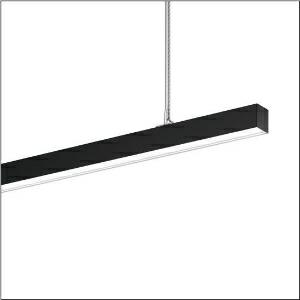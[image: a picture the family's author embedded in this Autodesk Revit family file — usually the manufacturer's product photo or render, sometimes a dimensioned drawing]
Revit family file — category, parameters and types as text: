
# Revit family: silica_21_51mx33da47bb
name_source: partatom
category: Lighting Fixtures
units: mm (PartAtom-declared; Revit-internal decimal feet)

## family parameters
Cut with Voids When Loaded = No
Host = Face
Light Source = No
Part Type = Normal
Room Calculation Point = No
Round Connector Dimension = Use Diameter
Shared = No

## types (1)
- --- (1 x LED, 5910 lm, 38.4 W, 4000K)
    Apparent Load = 38 VA
    CIE Flux Codes = 78 96 99 55 100
    Color Rendering = 80
    Color Temperature = 4000K
    Default Elevation = 1800 mm
    Description = Silica 21, office luminaire, primary optical cover: prismatic diffuser, of PMMA, CAT 2 (L<= 3000cd/m²), light emission: direct/indirect distribution, primary light characteristic: symmetric, installation type: suspended mounting, LED, rated luminous flux: 5.910lm, luminous efficacy: 154lm/W, light colour: 840, colour temperature: 4000K, control gear: DALI 2, with terminal, 3+2-pole, max. 2.5mm², mains connection: 220..240V, AC, 50/60Hz, rated input power: 38.4W, luminaire housing, of aluminium, matt jet black (RAL 9005), length: 1.204mm, width: 53mm, height: 53mm, protection rating (complete): IP20, insulation class (complete): insulation class I (protective earthing), certification: CE, permissible operating ambient temperature: 0..+35°C, standard: EN 50419, packaging unit: 1 piece
    Height = 53 mm
    Lamp = 1 x LED
    Lamp Light Flux = 5910 lm
    Lamp Power = 38.4 W
    Lamp count = 1
    Length = 1204 mm
    Luminous efficacy = 154 lm/W
    Manufacturer = Siteco
    ModVariant = No
    Model = 51MX33DA47BB
    Mounting Place = Ceiling
    Mounting Type = Pendant
    Number of Poles = 1
    OnlyDefault = Yes
    Power Factor = 1
    Product Name = Silica 21
    Product group = office luminaire | ceiling pendant
    ProductGroupID = 903
    Protection Class = Protection class I
    Protection Degree = IP 20
    RLX_Detail_Level = 1
    RLX_Emergency_Light_Flux = 0 lm
    RLX_Emergency_Type = 0
    RLX_Emergency_Type_DB = No
    RlxData = <blob elided: 25945 chars, md5=d487798e>
    Socket = socket
    Standby Power = 0 W
    System Light Flux = 5910 lm
    System Power = 38 W
    Type Comments = factory setting: luminous flux: 100 % | dim-lin: 254 | 322 mA
    Type Image = l_1335856.jpg
    URL = http://relux.com
    VarID = @adj_118921
    Voltage = 0 V
    Weight = 0.00 kg
    Width = 53 mm

## geometry (parser evidence)
native form markers: Blend x4, Sweep x15
no freeform markers — native parametric forms only
